FCSTD DOCUMENT  (FreeCAD 0.20R29177 (Git))
Label: HeatedBedV3
License: All rights reserved
LicenseURL: http://en.wikipedia.org/wiki/All_rights_reserved
objects: PartDesign::Plane×1, Sketcher::SketchObject×1, PartDesign::Body×1
note: 3 computed .brp shape members not serialized (recipe doc carries the construction recipe); baked Part::Feature solids carry a one-line shape summary decoded from their .brp

FEATURE [PartDesign::Plane] DatumPlane
  Length = 60
  ResizeMode = 0
  Width = 60
FEATURE [Sketcher::SketchObject] Sketch  label="PlanoHeatedBed"
  FullyConstrained = true
  MapMode = 5
  Support = -> [DatumPlane]
  sketch-geometry (106):
    g0: Circle CenterX=-104 CenterY=-104 CenterZ=0 NormalX=0 NormalY=0 NormalZ=1 AngleXU=0 Radius=1.5
    g1: Circle CenterX=104 CenterY=-104 CenterZ=0 NormalX=0 NormalY=0 NormalZ=1 AngleXU=0 Radius=1.5
    g2: Circle CenterX=104 CenterY=104 CenterZ=0 NormalX=0 NormalY=0 NormalZ=1 AngleXU=0 Radius=1.5
    g3: Circle CenterX=-104 CenterY=104 CenterZ=0 NormalX=0 NormalY=0 NormalZ=1 AngleXU=0 Radius=1.5
    g4: ArcOfCircle CenterX=104 CenterY=-104 CenterZ=0 NormalX=0 NormalY=0 NormalZ=1 AngleXU=0 Radius=10 StartAngle=4.01349 EndAngle=6.98209
    g5: ArcOfCircle CenterX=104 CenterY=104 CenterZ=0 NormalX=0 NormalY=0 NormalZ=1 AngleXU=0 Radius=10 StartAngle=5.58428 EndAngle=8.55288
    g6: ArcOfCircle CenterX=-104 CenterY=104 CenterZ=0 NormalX=0 NormalY=0 NormalZ=1 AngleXU=0 Radius=10 StartAngle=0.871894 EndAngle=3.8405
    g7: ArcOfCircle CenterX=-104 CenterY=-104 CenterZ=0 NormalX=0 NormalY=0 NormalZ=1 AngleXU=0 Radius=10 StartAngle=2.44269 EndAngle=5.41129
    g8: Circle CenterX=6 CenterY=6.5 CenterZ=0 NormalX=0 NormalY=0 NormalZ=1 AngleXU=0 Radius=1.05
    g9: Circle CenterX=6 CenterY=-6.5 CenterZ=0 NormalX=0 NormalY=0 NormalZ=1 AngleXU=0 Radius=1.05
    g10: Circle CenterX=-6 CenterY=6.5 CenterZ=0 NormalX=0 NormalY=0 NormalZ=1 AngleXU=0 Radius=1.05
    g11: Circle CenterX=-6 CenterY=-6.5 CenterZ=0 NormalX=0 NormalY=0 NormalZ=1 AngleXU=0 Radius=1.05
    g12: ArcOfCircle CenterX=174.203 CenterY=-45 CenterZ=0 NormalX=0 NormalY=0 NormalZ=1 AngleXU=0 Radius=81.7035 StartAngle=3.14159 EndAngle=3.8405
    g13: ArcOfCircle CenterX=45 CenterY=-174.203 CenterZ=0 NormalX=0 NormalY=0 NormalZ=1 AngleXU=0 Radius=81.7035 StartAngle=0.871894 EndAngle=1.5708
    g14: ArcOfCircle CenterX=-45 CenterY=-174.203 CenterZ=0 NormalX=0 NormalY=0 NormalZ=1 AngleXU=0 Radius=81.7035 StartAngle=1.5708 EndAngle=2.2697
    g15: ArcOfCircle CenterX=-174.203 CenterY=-45 CenterZ=0 NormalX=0 NormalY=0 NormalZ=1 AngleXU=0 Radius=81.7035 StartAngle=5.58428 EndAngle=6.28319
    g16: ArcOfCircle CenterX=-174.203 CenterY=45 CenterZ=0 NormalX=0 NormalY=0 NormalZ=1 AngleXU=0 Radius=81.7035 StartAngle=1e-16 EndAngle=0.698903
    g17: ArcOfCircle CenterX=-45 CenterY=174.203 CenterZ=0 NormalX=0 NormalY=0 NormalZ=1 AngleXU=0 Radius=81.7035 StartAngle=4.01349 EndAngle=4.71239
    g18: ArcOfCircle CenterX=174.203 CenterY=45 CenterZ=0 NormalX=0 NormalY=0 NormalZ=1 AngleXU=0 Radius=81.7035 StartAngle=2.44269 EndAngle=3.14159
    g19: ArcOfCircle CenterX=45 CenterY=174.203 CenterZ=0 NormalX=0 NormalY=0 NormalZ=1 AngleXU=0 Radius=81.7035 StartAngle=4.71239 EndAngle=5.41129
    g20: LineSegment StartX=-45 StartY=92.5 StartZ=0 EndX=45 EndY=92.5 EndZ=0
    g21: LineSegment StartX=92.5 StartY=45 StartZ=0 EndX=92.5 EndY=-45 EndZ=0
    g22: LineSegment StartX=-92.5 StartY=45 StartZ=0 EndX=-92.5 EndY=-45 EndZ=0
    g23: LineSegment StartX=-45 StartY=-92.5 StartZ=0 EndX=45 EndY=-92.5 EndZ=0
    g24: ArcOfCircle CenterX=-26.5 CenterY=-66.5 CenterZ=0 NormalX=0 NormalY=0 NormalZ=1 AngleXU=0 Radius=10 StartAngle=2.35619 EndAngle=4.71239
    g25: ArcOfCircle CenterX=0 CenterY=-40 CenterZ=0 NormalX=0 NormalY=0 NormalZ=1 AngleXU=0 Radius=10 StartAngle=0.785398 EndAngle=2.35619
    g26: ArcOfCircle CenterX=26.5 CenterY=-66.5 CenterZ=0 NormalX=0 NormalY=0 NormalZ=1 AngleXU=0 Radius=10 StartAngle=4.71239 EndAngle=7.06858
    g27: ArcOfCircle CenterX=40 CenterY=0 CenterZ=0 NormalX=0 NormalY=0 NormalZ=1 AngleXU=0 Radius=10 StartAngle=2.35619 EndAngle=3.92699
    g28: ArcOfCircle CenterX=66.5 CenterY=-26.5 CenterZ=0 NormalX=0 NormalY=0 NormalZ=1 AngleXU=0 Radius=10 StartAngle=3.92699 EndAngle=6.28319
    g29: ArcOfCircle CenterX=66.5 CenterY=26.5 CenterZ=0 NormalX=0 NormalY=0 NormalZ=1 AngleXU=0 Radius=10 StartAngle=0 EndAngle=2.35619
    g30: ArcOfCircle CenterX=-40 CenterY=0 CenterZ=0 NormalX=0 NormalY=0 NormalZ=1 AngleXU=0 Radius=10 StartAngle=5.49779 EndAngle=7.06858
    g31: ArcOfCircle CenterX=-66.5 CenterY=-26.5 CenterZ=0 NormalX=0 NormalY=0 NormalZ=1 AngleXU=0 Radius=10 StartAngle=3.14159 EndAngle=5.49779
    g32: ArcOfCircle CenterX=-66.5 CenterY=26.5 CenterZ=0 NormalX=0 NormalY=0 NormalZ=1 AngleXU=0 Radius=10 StartAngle=0.785398 EndAngle=3.14159
    g33: ArcOfCircle CenterX=0 CenterY=40 CenterZ=0 NormalX=0 NormalY=0 NormalZ=1 AngleXU=0 Radius=10 StartAngle=3.92699 EndAngle=5.49779
    g34: ArcOfCircle CenterX=26.5 CenterY=66.5 CenterZ=0 NormalX=0 NormalY=0 NormalZ=1 AngleXU=0 Radius=10 StartAngle=5.49779 EndAngle=7.85398
    g35: ArcOfCircle CenterX=-26.5 CenterY=66.5 CenterZ=0 NormalX=0 NormalY=0 NormalZ=1 AngleXU=0 Radius=10 StartAngle=1.5708 EndAngle=3.92699
    g36: LineSegment StartX=-26.5 StartY=-76.5 StartZ=0 EndX=26.5 EndY=-76.5 EndZ=0
    g37: LineSegment StartX=33.5711 StartY=-59.4289 StartZ=0 EndX=7.07107 EndY=-32.9289 EndZ=0
    g38: LineSegment StartX=-7.07107 StartY=-32.9289 StartZ=0 EndX=-33.5711 EndY=-59.4289 EndZ=0
    g39: LineSegment StartX=-59.4289 StartY=-33.5711 StartZ=0 EndX=-32.9289 EndY=-7.07107 EndZ=0
    g40: LineSegment StartX=-32.9289 StartY=7.07107 StartZ=0 EndX=-59.4289 EndY=33.5711 EndZ=0
    g41: LineSegment StartX=-76.5 StartY=26.5 StartZ=0 EndX=-76.5 EndY=-26.5 EndZ=0
    g42: LineSegment StartX=32.9289 StartY=-7.07107 StartZ=0 EndX=59.4289 EndY=-33.5711 EndZ=0
    g43: LineSegment StartX=76.5 StartY=-26.5 StartZ=0 EndX=76.5 EndY=26.5 EndZ=0
    g44: LineSegment StartX=59.4289 StartY=33.5711 StartZ=0 EndX=32.9289 EndY=7.07107 EndZ=0
    g45: LineSegment StartX=7.07107 StartY=32.9289 StartZ=0 EndX=33.5711 EndY=59.4289 EndZ=0
    g46: LineSegment StartX=26.5 StartY=76.5 StartZ=0 EndX=-26.5 EndY=76.5 EndZ=0
    g47: LineSegment StartX=-33.5711 StartY=59.4289 StartZ=0 EndX=-7.07107 EndY=32.9289 EndZ=0
    g48: LineSegment StartX=66.5 StartY=-26.5 StartZ=0 EndX=66.5 EndY=26.5 EndZ=0
    g49: LineSegment StartX=40 StartY=0 StartZ=0 EndX=66.5 EndY=0 EndZ=0
    g50: ArcOfCircle CenterX=30.6066 CenterY=30.6066 CenterZ=0 NormalX=0 NormalY=0 NormalZ=1 AngleXU=0 Radius=5 StartAngle=5.49779 EndAngle=8.63938
    g51: ArcOfCircle CenterX=20 CenterY=20 CenterZ=0 NormalX=0 NormalY=0 NormalZ=1 AngleXU=0 Radius=5 StartAngle=2.35619 EndAngle=5.49779
    g52: LineSegment StartX=27.0711 StartY=34.1421 StartZ=0 EndX=16.4645 EndY=23.5355 EndZ=0
    g53: LineSegment StartX=23.5355 StartY=16.4645 StartZ=0 EndX=34.1421 EndY=27.0711 EndZ=0
    g54: LineSegment StartX=51.8198 StartY=44.7487 StartZ=0 EndX=62.4264 EndY=55.3553 EndZ=0
    g55: ArcOfCircle CenterX=58.8909 CenterY=58.8909 CenterZ=0 NormalX=0 NormalY=0 NormalZ=1 AngleXU=0 Radius=5 StartAngle=5.49779 EndAngle=8.63938
    g56: LineSegment StartX=55.3553 StartY=62.4264 StartZ=0 EndX=44.7487 EndY=51.8198 EndZ=0
    g57: ArcOfCircle CenterX=48.2843 CenterY=48.2843 CenterZ=0 NormalX=0 NormalY=0 NormalZ=1 AngleXU=0 Radius=5 StartAngle=2.35619 EndAngle=5.49779
    g58: LineSegment StartX=23.5355 StartY=16.4645 StartZ=0 EndX=51.8198 EndY=44.7487 EndZ=0
    g59: LineSegment StartX=80.1041 StartY=73.033 StartZ=0 EndX=90.7107 EndY=83.6396 EndZ=0
    g60: ArcOfCircle CenterX=87.1751 CenterY=87.1751 CenterZ=0 NormalX=0 NormalY=0 NormalZ=1 AngleXU=0 Radius=5 StartAngle=5.49779 EndAngle=8.63938
    g61: LineSegment StartX=83.6396 StartY=90.7107 StartZ=0 EndX=73.033 EndY=80.1041 EndZ=0
    g62: ArcOfCircle CenterX=76.5685 CenterY=76.5685 CenterZ=0 NormalX=0 NormalY=0 NormalZ=1 AngleXU=0 Radius=5 StartAngle=2.35619 EndAngle=5.49779
    g63: LineSegment StartX=51.8198 StartY=44.7487 StartZ=0 EndX=80.1041 EndY=73.033 EndZ=0
    g64: ArcOfCircle CenterX=-30.6066 CenterY=30.6066 CenterZ=0 NormalX=0 NormalY=0 NormalZ=1 AngleXU=0 Radius=5 StartAngle=0.785398 EndAngle=3.92699
    g65: ArcOfCircle CenterX=-20 CenterY=20 CenterZ=0 NormalX=0 NormalY=0 NormalZ=1 AngleXU=0 Radius=5 StartAngle=3.92699 EndAngle=7.06858
    g66: LineSegment StartX=-34.1421 StartY=27.0711 StartZ=0 EndX=-23.5355 EndY=16.4645 EndZ=0
    g67: LineSegment StartX=-16.4645 StartY=23.5355 StartZ=0 EndX=-27.0711 EndY=34.1421 EndZ=0
    g68: ArcOfCircle CenterX=-20 CenterY=-20 CenterZ=0 NormalX=0 NormalY=0 NormalZ=1 AngleXU=0 Radius=5 StartAngle=5.49779 EndAngle=8.63938
    g69: ArcOfCircle CenterX=-30.6066 CenterY=-30.6066 CenterZ=0 NormalX=0 NormalY=0 NormalZ=1 AngleXU=0 Radius=5 StartAngle=2.35619 EndAngle=5.49779
    g70: LineSegment StartX=-23.5355 StartY=-16.4645 StartZ=0 EndX=-34.1421 EndY=-27.0711 EndZ=0
    g71: ArcOfCircle CenterX=20 CenterY=-20 CenterZ=0 NormalX=0 NormalY=0 NormalZ=1 AngleXU=0 Radius=5 StartAngle=0.785398 EndAngle=3.92699
    g72: ArcOfCircle CenterX=30.6066 CenterY=-30.6066 CenterZ=0 NormalX=0 NormalY=0 NormalZ=1 AngleXU=0 Radius=5 StartAngle=3.92699 EndAngle=7.06858
    g73: LineSegment StartX=16.4645 StartY=-23.5355 StartZ=0 EndX=27.0711 EndY=-34.1421 EndZ=0
    g74: LineSegment StartX=34.1421 StartY=-27.0711 StartZ=0 EndX=23.5355 EndY=-16.4645 EndZ=0
    g75: LineSegment StartX=-62.4264 StartY=55.3553 StartZ=0 EndX=-51.8198 EndY=44.7487 EndZ=0
    g76: LineSegment StartX=-44.7487 StartY=51.8198 StartZ=0 EndX=-55.3553 EndY=62.4264 EndZ=0
    g77: ArcOfCircle CenterX=-48.2843 CenterY=48.2843 CenterZ=0 NormalX=0 NormalY=0 NormalZ=1 AngleXU=0 Radius=5 StartAngle=3.92699 EndAngle=7.06858
    g78: ArcOfCircle CenterX=-58.8909 CenterY=58.8909 CenterZ=0 NormalX=0 NormalY=0 NormalZ=1 AngleXU=0 Radius=5 StartAngle=0.785398 EndAngle=3.92699
    g79: LineSegment StartX=-34.1421 StartY=27.0711 StartZ=0 EndX=-62.4264 EndY=55.3553 EndZ=0
    g80: LineSegment StartX=-90.7107 StartY=83.6396 StartZ=0 EndX=-80.1041 EndY=73.033 EndZ=0
    g81: LineSegment StartX=-73.033 StartY=80.1041 StartZ=0 EndX=-83.6396 EndY=90.7107 EndZ=0
    g82: ArcOfCircle CenterX=-76.5685 CenterY=76.5685 CenterZ=0 NormalX=0 NormalY=0 NormalZ=1 AngleXU=0 Radius=5 StartAngle=3.92699 EndAngle=7.06858
    g83: ArcOfCircle CenterX=-87.1751 CenterY=87.1751 CenterZ=0 NormalX=0 NormalY=0 NormalZ=1 AngleXU=0 Radius=5 StartAngle=0.785398 EndAngle=3.92699
    g84: LineSegment StartX=-62.4264 StartY=55.3553 StartZ=0 EndX=-90.7107 EndY=83.6396 EndZ=0
    g85: LineSegment StartX=-27.0711 StartY=-34.1421 StartZ=0 EndX=-16.4645 EndY=-23.5355 EndZ=0
    g86: LineSegment StartX=-51.8198 StartY=-44.7487 StartZ=0 EndX=-62.4264 EndY=-55.3553 EndZ=0
    g87: ArcOfCircle CenterX=-48.2843 CenterY=-48.2843 CenterZ=0 NormalX=0 NormalY=0 NormalZ=1 AngleXU=0 Radius=5 StartAngle=5.49779 EndAngle=8.63938
    g88: LineSegment StartX=-55.3553 StartY=-62.4264 StartZ=0 EndX=-44.7487 EndY=-51.8198 EndZ=0
    g89: ArcOfCircle CenterX=-58.8909 CenterY=-58.8909 CenterZ=0 NormalX=0 NormalY=0 NormalZ=1 AngleXU=0 Radius=5 StartAngle=2.35619 EndAngle=5.49779
    g90: LineSegment StartX=-80.1041 StartY=-73.033 StartZ=0 EndX=-90.7107 EndY=-83.6396 EndZ=0
    g91: ArcOfCircle CenterX=-76.5685 CenterY=-76.5685 CenterZ=0 NormalX=0 NormalY=0 NormalZ=1 AngleXU=0 Radius=5 StartAngle=5.49779 EndAngle=8.63938
    g92: LineSegment StartX=-83.6396 StartY=-90.7107 StartZ=0 EndX=-73.033 EndY=-80.1041 EndZ=0
    g93: ArcOfCircle CenterX=-87.1751 CenterY=-87.1751 CenterZ=0 NormalX=0 NormalY=0 NormalZ=1 AngleXU=0 Radius=5 StartAngle=2.35619 EndAngle=5.49779
    g94: ArcOfCircle CenterX=58.8909 CenterY=-58.8909 CenterZ=0 NormalX=0 NormalY=0 NormalZ=1 AngleXU=0 Radius=5 StartAngle=3.92699 EndAngle=7.06858
    g95: LineSegment StartX=62.4264 StartY=-55.3553 StartZ=0 EndX=51.8198 EndY=-44.7487 EndZ=0
    g96: LineSegment StartX=44.7487 StartY=-51.8198 StartZ=0 EndX=55.3553 EndY=-62.4264 EndZ=0
    g97: ArcOfCircle CenterX=48.2843 CenterY=-48.2843 CenterZ=0 NormalX=0 NormalY=0 NormalZ=1 AngleXU=0 Radius=5 StartAngle=0.785398 EndAngle=3.92699
    g98: LineSegment StartX=27.0711 StartY=-34.1421 StartZ=0 EndX=55.3553 EndY=-62.4264 EndZ=0
    g99: ArcOfCircle CenterX=87.1751 CenterY=-87.1751 CenterZ=0 NormalX=0 NormalY=0 NormalZ=1 AngleXU=0 Radius=5 StartAngle=3.92699 EndAngle=7.06858
    g100: LineSegment StartX=90.7107 StartY=-83.6396 StartZ=0 EndX=80.1041 EndY=-73.033 EndZ=0
    g101: LineSegment StartX=73.033 StartY=-80.1041 StartZ=0 EndX=83.6396 EndY=-90.7107 EndZ=0
    g102: ArcOfCircle CenterX=76.5685 CenterY=-76.5685 CenterZ=0 NormalX=0 NormalY=0 NormalZ=1 AngleXU=0 Radius=5 StartAngle=0.785398 EndAngle=3.92699
    g103: LineSegment StartX=55.3553 StartY=-62.4264 StartZ=0 EndX=83.6396 EndY=-90.7107 EndZ=0
    g104: LineSegment StartX=-34.1421 StartY=-27.0711 StartZ=0 EndX=-51.8198 EndY=-44.7487 EndZ=0
    g105: LineSegment StartX=-62.4264 StartY=-55.3553 StartZ=0 EndX=-80.1041 EndY=-73.033 EndZ=0
  constraints (249):
    c: Equal(g0,g3)
    c: Equal(g3,g2)
    c: Equal(g2,g1)
    c: Diameter(g2) = 3
    c: Symmetric(g1,g0,g-2)
    c: Symmetric(g2,g3,g-2)
    c: DistanceX(g0,g1) = 208
    c: DistanceY(g1,g2) = 208
    c: DistanceY(g0,g-1) = 104
    c: Coincident(g4,g1)
    c: Coincident(g5,g2)
    c: Coincident(g6,g3)
    c: Coincident(g7,g0)
    c: Equal(g9,g8)
    c: Equal(g8,g10)
    c: Equal(g10,g11)
    c: Diameter(g8) = 2.1
    c: Tangent(g4,g12) = 1.5708
    c: Tangent(g13,g4) = 1.5708
    c: Tangent(g14,g7) = 1.5708
    c: Tangent(g7,g15) = 1.5708
    c: Tangent(g5,g19) = 1.5708
    c: Tangent(g18,g5) = 1.5708
    c: Tangent(g6,g17) = 1.5708
    c: Tangent(g16,g6) = 1.5708
    c: Horizontal(g20)
    c: Vertical(g21)
    c: Vertical(g22)
    c: Horizontal(g23)
    c: Tangent(g23,g13) = 1.5708
    c: Tangent(g23,g14) = 1.5708
    c: Tangent(g12,g21) = -1.5708
    c: Tangent(g15,g22) = 1.5708
    c: Tangent(g18,g21) = -1.5708
    c: Tangent(g20,g19) = -1.5708
    c: Tangent(g17,g20) = -1.5708
    c: Tangent(g16,g22) = 1.5708
    c: Equal(g5,g6)
    c: Equal(g6,g7)
    c: Equal(g7,g4)
    c: Diameter(g4) = 20
    c: Symmetric(g13,g19,g-1)
    c: Symmetric(g12,g15,g-2)
    c: Equal(g15,g14)
    c: Equal(g14,g13)
    c: Equal(g12,g18)
    c: Equal(g18,g19)
    c: Equal(g19,g17)
    c: Equal(g17,g16)
    c: Symmetric(g11,g9,g-2)
    c: Symmetric(g8,g10,g-2)
    c: Symmetric(g9,g8,g-1)
    c: DistanceX(g11,g9) = 12
    c: DistanceY(g9,g8) = 13
    c: DistanceY(g13,g19) = 185
    c: DistanceX(g16,g18) = 185
    c: DistanceY(g15,g16) = 90
    c: PointOnObject(g25,g-2)
    c: PointOnObject(g27,g-1)
    c: PointOnObject(g30,g-1)
    c: PointOnObject(g33,g-2)
    c: Vertical(g43)
    c: Vertical(g41)
    c: Horizontal(g46)
    c: Horizontal(g36)
    c: Tangent(g36,g26) = -1.5708
    c: Tangent(g37,g26) = -1.5708
    c: Tangent(g24,g36) = -1.5708
    c: Tangent(g38,g24) = -1.5708
    c: Tangent(g38,g25) = -1.5708
    c: Tangent(g37,g25) = -1.5708
    c: Tangent(g40,g32) = -1.5708
    c: Tangent(g40,g30) = -1.5708
    c: Tangent(g39,g30) = -1.5708
    c: Tangent(g39,g31) = -1.5708
    c: Tangent(g41,g31) = -1.5708
    c: Tangent(g41,g32) = -1.5708
    c: Tangent(g42,g28) = -1.5708
    c: Tangent(g43,g28) = -1.5708
    c: Tangent(g43,g29) = -1.5708
    c: Tangent(g44,g29) = -1.5708
    c: Tangent(g44,g27) = -1.5708
    c: Tangent(g42,g27) = -1.5708
    c: Tangent(g45,g33) = -1.5708
    c: Tangent(g47,g33) = -1.5708
    c: Tangent(g45,g34) = -1.5708
    c: Tangent(g46,g34) = -1.5708
    c: Tangent(g46,g35) = -1.5708
    c: Tangent(g47,g35) = -1.5708
    c: Equal(g24,g25)
    c: Equal(g27,g29)
    c: Equal(g32,g30)
    c: Equal(g33,g35)
    c: Symmetric(g26,g24,g-2)
    c: Symmetric(g28,g29,g-1)
    c: Symmetric(g31,g32,g-1)
    c: Symmetric(g35,g34,g-2)
    c: Equal(g28,g26)
    c: Equal(g29,g34)
    c: Equal(g32,g35)
    c: DistanceY(g25,g-1) = 40
    c: DistanceX(g-1,g27) = 40
    c: DistanceX(g30,g-1) = 40
    c: DistanceY(g-1,g33) = 40
    c: DistanceY(g13,g26) = 16
    c: DistanceX(g28,g12) = 16
    c: Symmetric(g31,g28,g-2)
    c: Symmetric(g24,g35,g-1)
    c: Angle(g37) = 2.35619
    c: Diameter(g26) = 20
    c: Coincident(g48,g28)
    c: Coincident(g48,g29)
    c: Coincident(g49,g27)
    c: PointOnObject(g49,g48)
    c: Horizontal(g49)
    c: DistanceY(g28,g49) = 26.5
    c: Tangent(g50,g52) = -1.5708
    c: Tangent(g52,g51) = -1.5708
    c: Tangent(g51,g53) = -1.5708
    c: Tangent(g53,g50) = -1.5708
    c: Equal(g50,g51)
    c: Angle(g53) = 0.785398
    c: Tangent(g55,g56) = -1.5708
    c: Tangent(g56,g57) = -1.5708
    c: Tangent(g57,g54) = -1.5708
    c: Tangent(g54,g55) = -1.5708
    c: Equal(g55,g57)
    c: Angle(g54) = 0.785398
    c: Coincident(g53,g58)
    c: Coincident(g54,g58)
    c: Distance(g58) = 40
    c: Angle(g58) = 0.785398
    c: Tangent(g60,g61) = -1.5708
    c: Tangent(g61,g62) = -1.5708
    c: Tangent(g62,g59) = -1.5708
    c: Tangent(g59,g60) = -1.5708
    c: Equal(g60,g62)
    c: Angle(g59) = 0.785398
    c: Coincident(g54,g63)
    c: Coincident(g59,g63)
    c: Equal(g58,g63)
    c: Parallel(g63,g58)
    c: Diameter(g51) = 10
    c: Equal(g57,g51)
    c: Equal(g51,g62)
    c: DistanceX(g-1,g51) = 20
    c: DistanceY(g-1,g51) = 20
    c: Distance(g50,g51) = 15
    c: Distance(g57,g55) = 15
    c: Distance(g62,g60) = 15
    c: Tangent(g64,g66) = -1.5708
    c: Tangent(g66,g65) = -1.5708
    c: Tangent(g65,g67) = -1.5708
    c: Tangent(g67,g64) = -1.5708
    c: Equal(g64,g65)
    c: Tangent(g68,g70) = -1.5708
    c: Tangent(g70,g69) = -1.5708
    c: Equal(g68,g69)
    c: Tangent(g71,g73) = -1.5708
    c: Tangent(g73,g72) = -1.5708
    c: Tangent(g72,g74) = -1.5708
    c: Tangent(g74,g71) = -1.5708
    c: Equal(g71,g72)
    c: Angle(g67) = 2.35619
    c: Angle(g70) = -2.35619
    c: Angle(g74) = 2.35619
    c: Equal(g51,g71)
    c: Equal(g71,g68)
    c: Equal(g68,g65)
    c: Symmetric(g51,g65,g-2)
    c: Symmetric(g68,g71,g-2)
    c: Symmetric(g68,g65,g-1)
    c: Tangent(g78,g75) = -1.5708
    c: Tangent(g75,g77) = -1.5708
    c: Tangent(g77,g76) = -1.5708
    c: Tangent(g76,g78) = -1.5708
    c: Equal(g78,g77)
    c: Angle(g76) = 2.35619
    c: Coincident(g66,g79)
    c: Coincident(g75,g79)
    c: Distance(g79) = 40
    c: Angle(g79) = 2.35619
    c: Tangent(g83,g80) = -1.5708
    c: Tangent(g80,g82) = -1.5708
    c: Tangent(g82,g81) = -1.5708
    c: Tangent(g81,g83) = -1.5708
    c: Equal(g83,g82)
    c: Angle(g81) = 2.35619
    c: Coincident(g75,g84)
    c: Coincident(g80,g84)
    c: Equal(g79,g84)
    c: Parallel(g84,g79)
    c: Tangent(g85,g68) = -1.5708
    c: Tangent(g85,g69) = -1.5708
    c: Tangent(g87,g86) = -1.5708
    c: Tangent(g86,g89) = -1.5708
    c: Equal(g87,g89)
    c: Angle(g86) = -2.35619
    c: Tangent(g88,g87) = -1.5708
    c: Tangent(g88,g89) = -1.5708
    c: Tangent(g91,g90) = -1.5708
    c: Tangent(g90,g93) = -1.5708
    c: Equal(g91,g93)
    c: Angle(g90) = -2.35619
    c: Tangent(g92,g91) = -1.5708
    c: Tangent(g92,g93) = -1.5708
    c: Tangent(g97,g96) = -1.5708
    c: Tangent(g96,g94) = -1.5708
    c: Tangent(g94,g95) = -1.5708
    c: Tangent(g95,g97) = -1.5708
    c: Equal(g97,g94)
    c: Angle(g95) = 2.35619
    c: Coincident(g72,g98)
    c: Coincident(g94,g98)
    c: Distance(g98) = 40
    c: Angle(g98) = -0.785398
    c: Tangent(g102,g101) = -1.5708
    c: Tangent(g101,g99) = -1.5708
    c: Tangent(g99,g100) = -1.5708
    c: Tangent(g100,g102) = -1.5708
    c: Equal(g102,g99)
    c: Angle(g100) = 2.35619
    c: Coincident(g94,g103)
    c: Coincident(g99,g103)
    c: Equal(g98,g103)
    c: Parallel(g103,g98)
    c: Coincident(g104,g69)
    c: Coincident(g104,g86)
    c: Coincident(g105,g86)
    c: Coincident(g105,g90)
    c: Equal(g87,g69)
    c: Equal(g91,g89)
    c: Angle(g104) = -2.35619
    c: Angle(g105) = -2.35619
    c: Equal(g97,g72)
    c: Equal(g94,g102)
    c: Equal(g77,g64)
    c: Equal(g78,g82)
    c: Distance(g65,g64) = 15
    c: Distance(g78,g77) = 15
    c: Distance(g82,g83) = 15
    c: Distance(g69,g68) = 15
    c: Distance(g89,g87) = 15
    c: Distance(g91,g93) = 15
    c: Distance(g89,g69) = 40
    c: Distance(g93,g89) = 40
    c: Distance(g71,g72) = 15
    c: Distance(g102,g99) = 15
    c: Distance(g94,g97) = 15
FEATURE [PartDesign::Body] Body
  Group = -> [DatumPlane,Sketch]
  Origin = -> Origin
